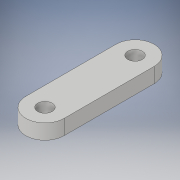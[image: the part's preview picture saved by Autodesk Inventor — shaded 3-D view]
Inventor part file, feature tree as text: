
AUTODESK INVENTOR PART (.ipt)
format: ipt  version: 2019.4 (Build 234330000, 330)  size: 141,824 bytes
history: native  units: mm
features: sketch x5, extrude x2, hole x1, thicken_offset x1
ambient origin geometry x8: Origin, YZ Plane, XZ Plane, XY Plane, X Axis, Y Axis, Z Axis, Center Point
bodies: Solid1 (feature_tree)
feature tree (9):
  extrude  "Extrusion1"  Depth=5.31mm
  sketch  "Sketch2"  dims[d8=33.0mm d9=5.31mm]
  extrude  "Extrusion2"  Depth=5.31mm
  sketch  "Sketch4"  dims[d13=90.0deg]
  sketch  "Sketch5"  dims[d14=33.0mm d15=3.8mm d16=32.9mm d17=3.8mm d18=1.2mm d19=0.0mm d20=5.1mm d21=33.3mm d22=5.31mm d23=2.0mm d24=0.525344mm d25=4.0mm d26=20.594885mm d27=2.0mm d28=2.0mm]
  hole  "Hole1"  [1 undecoded]
  thicken_offset  "Thicken1"
  sketch  "Sketch1"  dims[d5=5.5mm d6=0.0mm d7=5.31mm]
  sketch  "Sketch3"  dims[d11=33.0mm d12=5.0mm]
note: 1 required parameter value undecoded (feature->parameter linkage not recoverable at this tier; creation-order binding heuristic only, values carry confidence <= 0.55)
